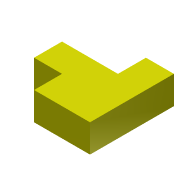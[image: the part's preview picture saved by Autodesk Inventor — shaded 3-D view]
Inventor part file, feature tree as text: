
AUTODESK INVENTOR PART (.ipt)
format: ipt  version: 2015 (Build 190159000, 159)  size: 80,896 bytes
history: native  units: in
note: dims shown in document units (in); Inventor stores cm internally (conversion verified against a paired STEP export)
features: extrude x1, sketch x1
ambient origin geometry x8: Origin, YZ Plane, XZ Plane, XY Plane, X Axis, Y Axis, Z Axis, Center Point
bodies: Solid1 (feature_tree)
feature tree (2):
  extrude  "Extrusion1"  Depth=1.0in
  sketch  "Sketch1"  dims[d0=2.0in d1=1.0in d2=1.0in d3=1.0in d4=1.0in d5=2.0in d6=1.0in d7=0.0in]
